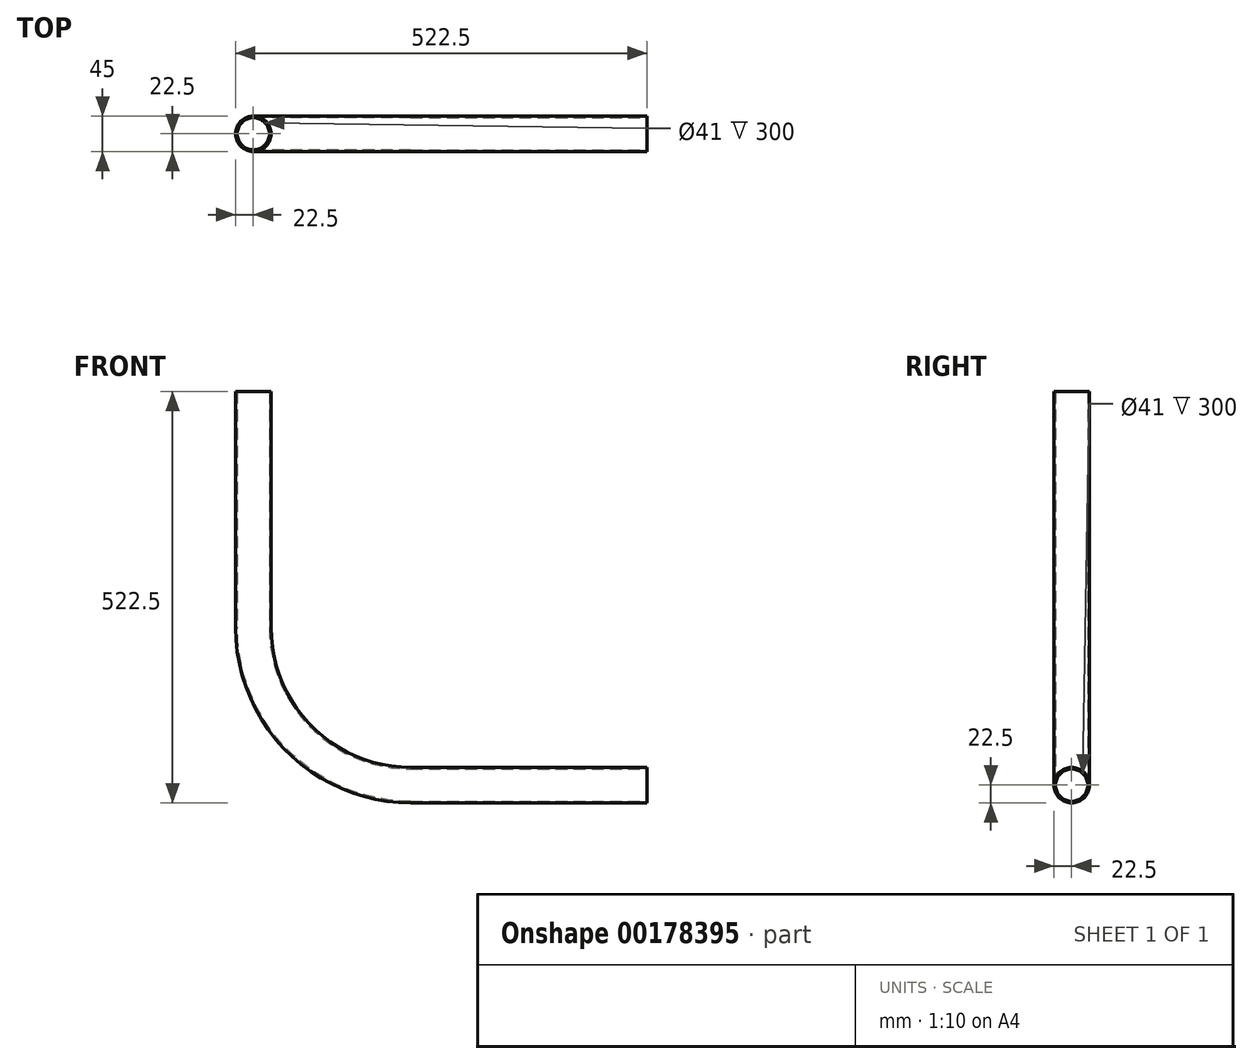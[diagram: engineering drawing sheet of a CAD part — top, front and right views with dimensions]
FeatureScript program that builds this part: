
annotation { "Feature Type Name" : "Feature", "Feature Type Description" : "" }
export const myFeature = defineFeature(function(context is Context, id is Id, definition is map)
    precondition{}
    {
        {
            var Q0;
            Q0=qCreatedBy(makeId("Front.planeOp"),FACE);
            var sketch = newSketch(context, id + "F0", { "sketchPlane" : qUnion([Q0])});
            skLineSegment(sketch, "E0", {"start": v(0, 200) * mm, "end": v(0, 500) * mm});
            skLineSegment(sketch, "E1", {"start": v(200, 0) * mm, "end": v(500, 0) * mm});
            skPoint(sketch, "E2.visualSharp", {"position": v(0, 0) * mm});
            skArc(sketch, "E2.filletArc", {"start": v(0, 200) * mm, "mid": v(58.58, 58.58) * mm, "end": v(200, 0) * mm});
            skSolve(sketch);
        }
        {
            var Q0;
            Q0=sQuery(id+"F0.wireOp",VERTEX,"E0.end");
            var Q1;
            Q1=qCreatedBy(makeId("Top.planeOp"),FACE);
            cPlane(context, id + "F1", {"entities" : qUnion([Q0, Q1]), "cplaneType" : CPlaneType.PLANE_POINT, "offset" : 25 * mm, "width" : 150 * mm, "height" : 150 * mm});
        }
        {
            var Q0;
            Q0=qCreatedBy(id+"F1.planeOp",FACE);
            var sketch = newSketch(context, id + "F2", { "sketchPlane" : qUnion([Q0])});
            skCircle(sketch, "E3", {"center": v(0, 0) * mm, "radius": 22.5 * mm});
            skCircle(sketch, "E4.0", {"center": v(0, 0) * mm, "radius": 20.5 * mm});
            skSolve(sketch);
        }
        {
            var Q0;
            Q0=makeQuery(id+"F2.imprint","IMPRINT",FACE,{"disambiguationData":[TD([[makeQuery(id+"F2.imprint","IMPRINT",EDGE,{"derivedFrom":sQuery(id+"F2.wireOp",EDGE,"E3")}),1.0]])]});
            var Q1;
            Q1=sQuery(id+"F0.wireOp",EDGE,"E0");
            var Q2;
            Q2=sQuery(id+"F0.wireOp",EDGE,"E2.filletArc");
            var Q3;
            Q3=sQuery(id+"F0.wireOp",EDGE,"E1");
            sweep(context, id + "F3", {"profiles" : qUnion([Q0]), "path" : qUnion([Q1, Q2, Q3])});
        }
    });
